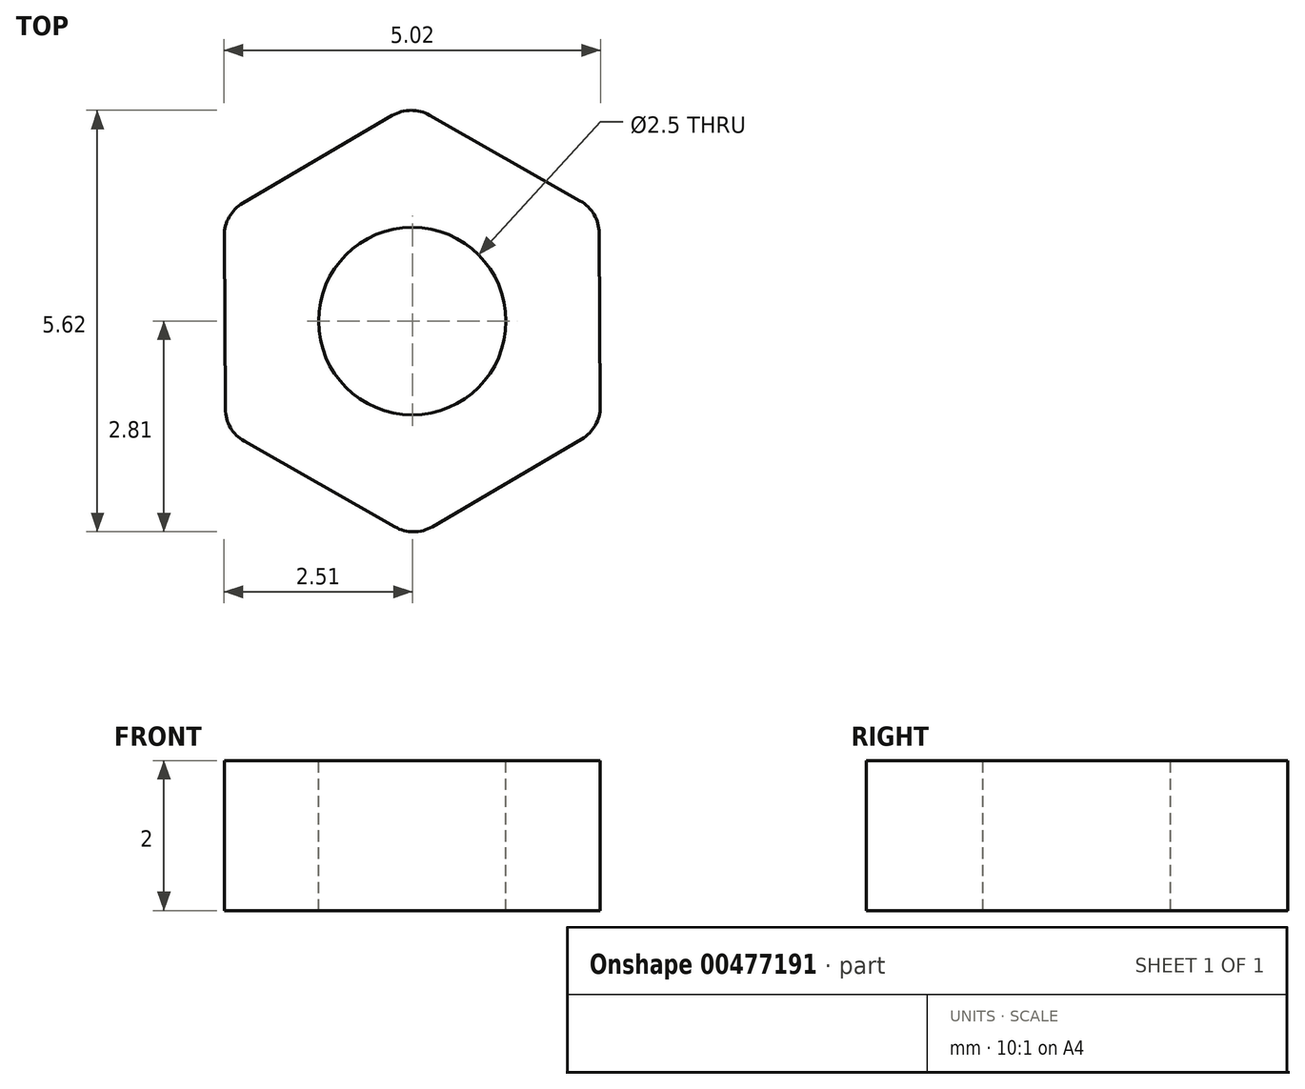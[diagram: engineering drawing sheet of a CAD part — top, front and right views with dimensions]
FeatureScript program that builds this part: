
annotation { "Feature Type Name" : "Feature", "Feature Type Description" : "" }
export const myFeature = defineFeature(function(context is Context, id is Id, definition is map)
    precondition{}
    {
        {
            var Q0;
            Q0=qCreatedBy(makeId("Top.planeOp"),FACE);
            var sketch = newSketch(context, id + "F0", { "sketchPlane" : qUnion([Q0])});
            skCircle(sketch, "E0.cCircle", {"center": v(0, 0) * mm, "radius": 5 * mm, "construction": true});
            skLineSegment(sketch, "E0.0", {"start": v(5.02, -2.85) * mm, "end": v(0.04, -5.77) * mm});
            skLineSegment(sketch, "E0.1", {"start": v(0.04, -5.77) * mm, "end": v(-4.98, -2.92) * mm});
            skLineSegment(sketch, "E0.2", {"start": v(-4.98, -2.92) * mm, "end": v(-5.02, 2.85) * mm});
            skLineSegment(sketch, "E0.3", {"start": v(-5.02, 2.85) * mm, "end": v(-0.04, 5.77) * mm});
            skLineSegment(sketch, "E0.4", {"start": v(-0.04, 5.77) * mm, "end": v(4.98, 2.92) * mm});
            skLineSegment(sketch, "E0.5", {"start": v(4.98, 2.92) * mm, "end": v(5.02, -2.85) * mm});
            skPoint(sketch, "E0.0.midPoint", {"position": v(2.53, -4.31) * mm});
            skSolve(sketch);
        }
        {
            var Q0;
            Q0=qSketchRegion(id+"F0",true);
            extrude(context, id + "F1", {"entities" : qUnion([Q0]), "depth" : 4 * mm});
        }
        {
            var Q0;
            Q0=makeQuery(id+"F1.opExtrude","CAP_FACE",FACE,{"disambiguationData":[OSD([sQuery(id+"F0.wireOp",EDGE,"E0.0"),sQuery(id+"F0.wireOp",EDGE,"E0.1"),sQuery(id+"F0.wireOp",EDGE,"E0.2"),sQuery(id+"F0.wireOp",EDGE,"E0.3"),sQuery(id+"F0.wireOp",EDGE,"E0.4"),sQuery(id+"F0.wireOp",EDGE,"E0.5")])],"isStart":false});
            var sketch = newSketch(context, id + "F2", { "sketchPlane" : qUnion([Q0])});
            skCircle(sketch, "E1", {"center": v(0, 0) * mm, "radius": 2.5 * mm});
            skSolve(sketch);
        }
        {
            var Q0;
            Q0=sQuery(id+"F2.wireOp",VERTEX,"E1.center");
            var Q1;
            Q1=makeQuery(id+"F1.opExtrude","SWEPT_BODY",BODY,{"disambiguationData":[OSD([sQuery(id+"F0.wireOp",EDGE,"E0.0"),sQuery(id+"F0.wireOp",EDGE,"E0.1"),sQuery(id+"F0.wireOp",EDGE,"E0.2"),sQuery(id+"F0.wireOp",EDGE,"E0.3"),sQuery(id+"F0.wireOp",EDGE,"E0.4"),sQuery(id+"F0.wireOp",EDGE,"E0.5")])]});
            hole(context, id + "F3", {"style" : HoleStyle.SIMPLE, "endStyle" : HoleEndStyle.BLIND, "holeDiameter" : 5 * mm, "holeDepth" : 10 * mm, "isTappedThrough" : true, "tappedDepth" : 12 * mm, "tapClearance" : 3, "locations" : qUnion([Q0]), "scope" : qUnion([Q1])});
        }
        {
            var Q0;
            Q0=makeQuery(id+"F1.opExtrude","SWEPT_EDGE",EDGE,{"disambiguationData":[OSD([sQuery(id+"F0.wireOp",EDGE,"E0.2"),sQuery(id+"F0.wireOp",EDGE,"E0.3")])]});
            var Q1;
            Q1=makeQuery(id+"F1.opExtrude","SWEPT_EDGE",EDGE,{"disambiguationData":[OSD([sQuery(id+"F0.wireOp",EDGE,"E0.3"),sQuery(id+"F0.wireOp",EDGE,"E0.4")])]});
            var Q2;
            Q2=makeQuery(id+"F1.opExtrude","SWEPT_EDGE",EDGE,{"disambiguationData":[OSD([sQuery(id+"F0.wireOp",EDGE,"E0.1"),sQuery(id+"F0.wireOp",EDGE,"E0.2")])]});
            var Q3;
            Q3=makeQuery(id+"F1.opExtrude","SWEPT_EDGE",EDGE,{"disambiguationData":[OSD([sQuery(id+"F0.wireOp",EDGE,"E0.0"),sQuery(id+"F0.wireOp",EDGE,"E0.1")])]});
            var Q4;
            Q4=makeQuery(id+"F1.opExtrude","SWEPT_EDGE",EDGE,{"disambiguationData":[OSD([sQuery(id+"F0.wireOp",EDGE,"E0.0"),sQuery(id+"F0.wireOp",EDGE,"E0.5")])]});
            var Q5;
            Q5=makeQuery(id+"F1.opExtrude","SWEPT_EDGE",EDGE,{"disambiguationData":[OSD([sQuery(id+"F0.wireOp",EDGE,"E0.4"),sQuery(id+"F0.wireOp",EDGE,"E0.5")])]});
            fillet(context, id + "F4", {"entities" : qUnion([Q0, Q1, Q2, Q3, Q4, Q5]), "radius" : 1 * mm, "tangentPropagation" : true, "allowEdgeOverflow" : false});
        }
        {
            var Q0;
            Q0=makeQuery(id+"F1.opExtrude","SWEPT_BODY",BODY,{"disambiguationData":[OSD([sQuery(id+"F0.wireOp",EDGE,"E0.0"),sQuery(id+"F0.wireOp",EDGE,"E0.1"),sQuery(id+"F0.wireOp",EDGE,"E0.2"),sQuery(id+"F0.wireOp",EDGE,"E0.3"),sQuery(id+"F0.wireOp",EDGE,"E0.4"),sQuery(id+"F0.wireOp",EDGE,"E0.5")])]});
            var Q1;
            Q1=qCreatedBy(makeId("Origin.pointOp"),VERTEX);
            transform(context, id + "F5", {"entities" : qUnion([Q0]), "transformType" : TransformType.SCALE_UNIFORMLY, "scale" : .5, "scalePoint" : qUnion([Q1]), "makeCopy" : false});
        }
    });
